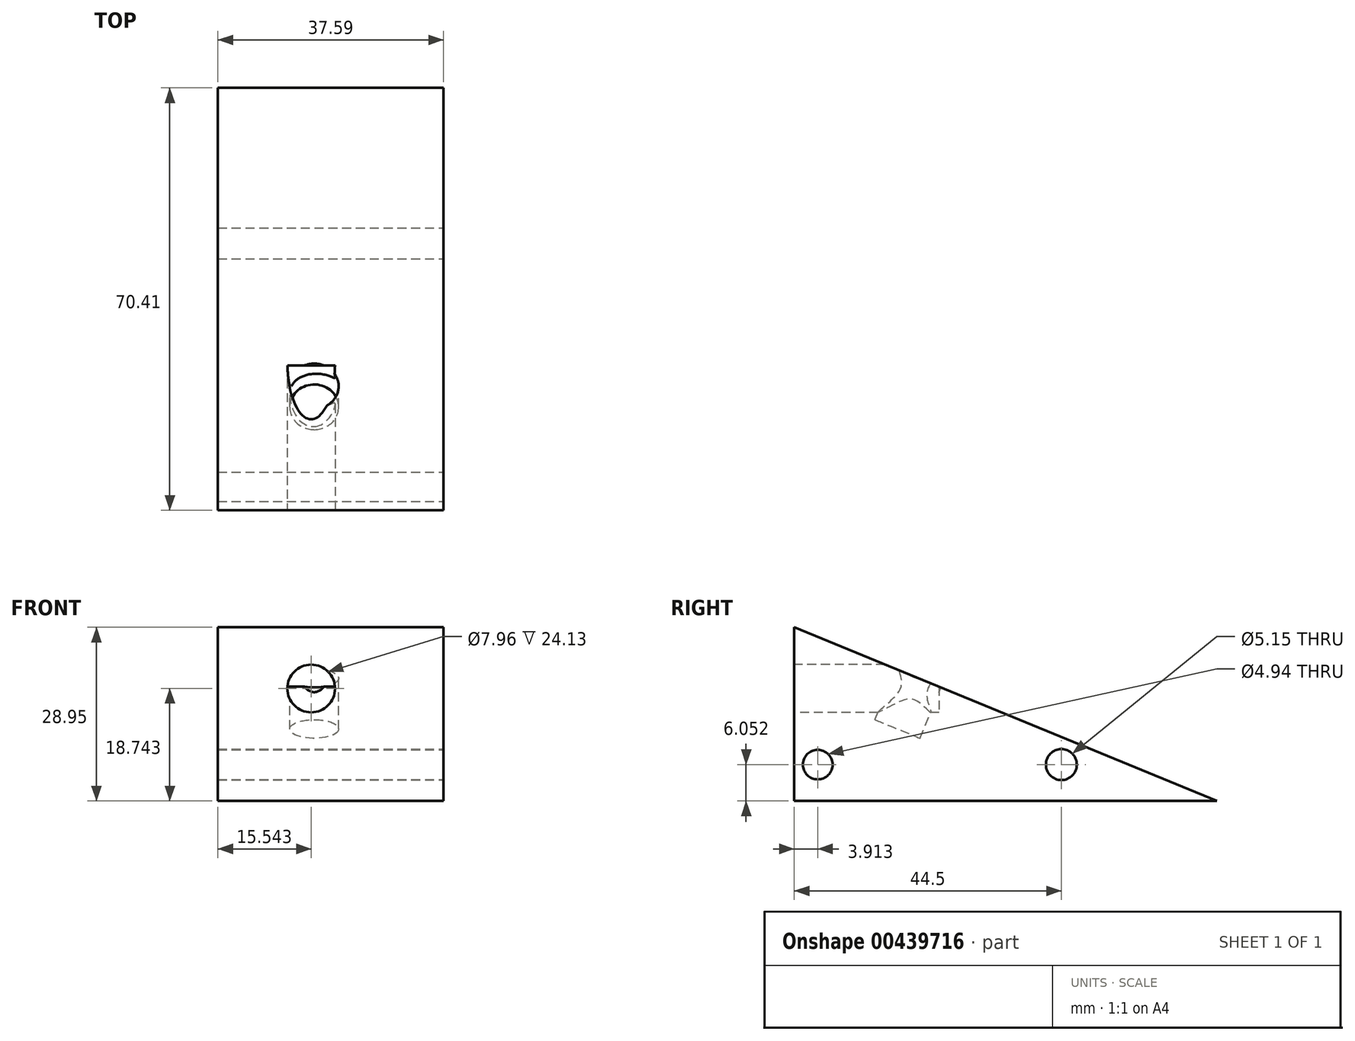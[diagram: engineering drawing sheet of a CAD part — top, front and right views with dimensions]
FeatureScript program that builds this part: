
annotation { "Feature Type Name" : "Feature", "Feature Type Description" : "" }
export const myFeature = defineFeature(function(context is Context, id is Id, definition is map)
    precondition{}
    {
        {
            var Q0;
            Q0=qCreatedBy(makeId("Right.planeOp"),FACE);
            var sketch = newSketch(context, id + "F0", { "sketchPlane" : qUnion([Q0])});
            skLineSegment(sketch, "E0", {"start": v(-44.5, 34.6) * mm, "end": v(-44.5, 5.64) * mm});
            skLineSegment(sketch, "E1", {"start": v(-44.5, 5.64) * mm, "end": v(25.9, 5.64) * mm});
            skLineSegment(sketch, "E2", {"start": v(25.9, 5.64) * mm, "end": v(-44.5, 34.6) * mm});
            skSolve(sketch);
        }
        {
            var Q0;
            Q0 = qSketchRegion(id + "F0", true);
            extrude(context, id + "F1", {"entities" : qUnion([Q0]), "depth" : 25.4 * mm});
        }
        {
            var Q0;
            Q0=makeQuery(id+"F1.opExtrude","CAP_FACE",FACE,{"disambiguationData":[OSD([sQuery(id+"F0.wireOp",EDGE,"E0"),sQuery(id+"F0.wireOp",EDGE,"E1"),sQuery(id+"F0.wireOp",EDGE,"E2")])],"isStart":true});
            extrude(context, id + "F2", {"entities" : qUnion([Q0]), "operationType" : NewBodyOperationType.ADD, "depth" : 12.2 * mm});
        }
        {
            var Q0;
            Q0=makeQuery(id+"F1.opExtrude","CAP_FACE",FACE,{"disambiguationData":[OSD([sQuery(id+"F0.wireOp",EDGE,"E0"),sQuery(id+"F0.wireOp",EDGE,"E1"),sQuery(id+"F0.wireOp",EDGE,"E2")])],"isStart":false});
            var sketch = newSketch(context, id + "F3", { "sketchPlane" : qUnion([Q0])});
            skCircle(sketch, "E3", {"center": v(-40.59, 11.7) * mm, "radius": 2.47 * mm});
            skCircle(sketch, "E4", {"center": v(0, 11.7) * mm, "radius": 2.57 * mm});
            skSolve(sketch);
        }
        {
            var Q0;
            Q0=makeQuery(id+"F3.imprint","IMPRINT",FACE,{"disambiguationData":[TD([[makeQuery(id+"F3.imprint","IMPRINT",EDGE,{"derivedFrom":sQuery(id+"F3.wireOp",EDGE,"E3")}),1.0]])]});
            var Q1;
            Q1=makeQuery(id+"F3.imprint","IMPRINT",FACE,{"disambiguationData":[TD([[makeQuery(id+"F3.imprint","IMPRINT",EDGE,{"derivedFrom":sQuery(id+"F3.wireOp",EDGE,"E4")}),1.0]])]});
            extrude(context, id + "F4", {"entities" : qUnion([Q0, Q1]), "operationType" : NewBodyOperationType.REMOVE, "oppositeDirection" : true, "depth" : 43.18 * mm});
        }
        {
            var Q0;
            {var subQ0=sQuery(id+"F0.wireOp",EDGE,"E2");Q0=makeQuery(id+"F2.boolean.opBoolean","MERGE",FACE,{"derivedFrom":[makeQuery(id+"F1.opExtrude","SWEPT_FACE",FACE,{"disambiguationData":[OSD([subQ0])]}),makeQuery(id+"F2.opExtrude","SWEPT_FACE",FACE,{"disambiguationData":[OSD([subQ0])]})]});}
            var sketch = newSketch(context, id + "F5", { "sketchPlane" : qUnion([Q0])});
            skCircle(sketch, "E5", {"center": v(3.85, -31.95) * mm, "radius": 4.07 * mm});
            skSolve(sketch);
        }
        {
            var Q0;
            Q0 = qSketchRegion(id + "F5", true);
            extrude(context, id + "F6", {"entities" : qUnion([Q0]), "operationType" : NewBodyOperationType.REMOVE, "oppositeDirection" : true, "depth" : 9.14 * mm});
        }
        {
            var Q0;
            {var subQ0=sQuery(id+"F0.wireOp",EDGE,"E0");Q0=makeQuery(id+"F2.boolean.opBoolean","MERGE",FACE,{"derivedFrom":[makeQuery(id+"F1.opExtrude","SWEPT_FACE",FACE,{"disambiguationData":[OSD([subQ0])]}),makeQuery(id+"F2.opExtrude","SWEPT_FACE",FACE,{"disambiguationData":[OSD([subQ0])]})]});}
            var sketch = newSketch(context, id + "F7", { "sketchPlane" : qUnion([Q0])});
            skCircle(sketch, "E6", {"center": v(3.35, 24.38) * mm, "radius": 3.98 * mm});
            skSolve(sketch);
        }
        {
            var Q0;
            Q0 = qSketchRegion(id + "F7", true);
            extrude(context, id + "F8", {"entities" : qUnion([Q0]), "operationType" : NewBodyOperationType.REMOVE, "oppositeDirection" : true, "depth" : 24.13 * mm});
        }
    });
